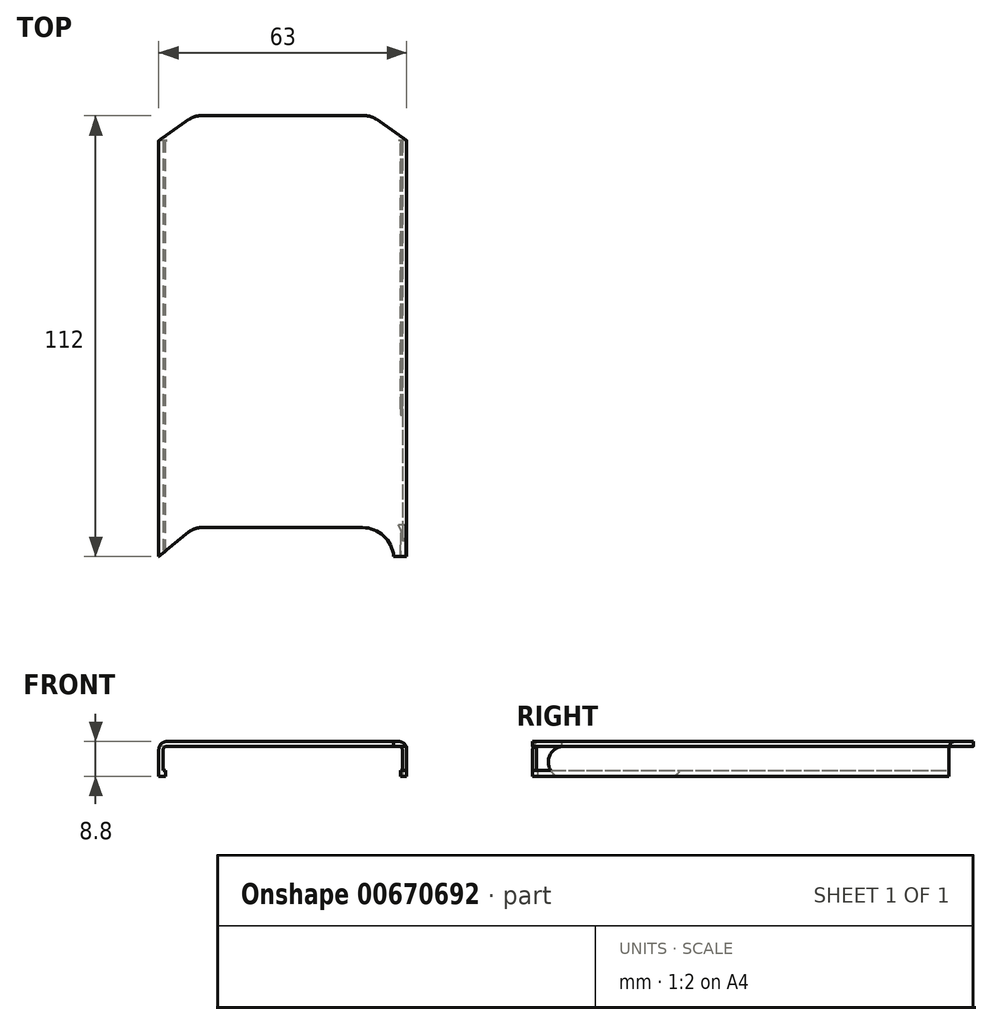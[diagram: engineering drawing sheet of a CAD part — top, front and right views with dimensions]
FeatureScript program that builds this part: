
annotation { "Feature Type Name" : "Feature", "Feature Type Description" : "" }
export const myFeature = defineFeature(function(context is Context, id is Id, definition is map)
    precondition{}
    {
        {
            var Q0;
            Q0=qCreatedBy(makeId("Top.planeOp"),FACE);
            var sketch = newSketch(context, id + "F0", { "sketchPlane" : qUnion([Q0])});
            skLineSegment(sketch, "E0", {"start": v(0, 105.7) * mm, "end": v(7.7, 111.1) * mm});
            skLineSegment(sketch, "E1", {"start": v(10.58, 112) * mm, "end": v(31.5, 112) * mm});
            skLineSegment(sketch, "E2.MirrorCS", {"start": v(52.42, 112) * mm, "end": v(31.5, 112) * mm});
            skLineSegment(sketch, "E3.MirrorCS", {"start": v(63, 105.7) * mm, "end": v(55.3, 111.1) * mm});
            skCircle(sketch, "E4", {"center": v(51.72, -0.65) * mm, "radius": 8 * mm, "construction": true});
            skLineSegment(sketch, "E5", {"start": v(63, 0) * mm, "end": v(59.7, 0) * mm});
            skLineSegment(sketch, "E6", {"start": v(51.72, 7.35) * mm, "end": v(10.78, 7.35) * mm});
            skLineSegment(sketch, "E7", {"start": v(7.62, 6.22) * mm, "end": v(0, 0) * mm});
            skArc(sketch, "E8", {"start": v(59.7, 0) * mm, "mid": v(57.14, 5.23) * mm, "end": v(51.72, 7.35) * mm});
            skPoint(sketch, "E9.visualSharp", {"position": v(9, 7.35) * mm});
            skArc(sketch, "E9.filletArc", {"start": v(10.78, 7.35) * mm, "mid": v(9.1, 7.06) * mm, "end": v(7.62, 6.22) * mm});
            skPoint(sketch, "E10.visualSharp", {"position": v(9, 112) * mm});
            skArc(sketch, "E10.filletArc", {"start": v(10.58, 112) * mm, "mid": v(9.07, 111.77) * mm, "end": v(7.7, 111.1) * mm});
            skPoint(sketch, "E11.visualSharp", {"position": v(54, 112) * mm});
            skArc(sketch, "E11.filletArc", {"start": v(55.3, 111.1) * mm, "mid": v(53.93, 111.77) * mm, "end": v(52.42, 112) * mm});
            skLineSegment(sketch, "E12", {"start": v(0, 0) * mm, "end": v(0, 105.7) * mm});
            skLineSegment(sketch, "E13", {"start": v(63, 105.7) * mm, "end": v(63, 0) * mm});
            skSolve(sketch);
        }
        {
            var Q0;
            Q0 = qSketchRegion(id + "F0", true);
            extrude(context, id + "F1", {"entities" : qUnion([Q0]), "depth" : 1.2 * mm, "offsetDistance" : 25 * mm});
        }
        {
            var Q0;
            Q0=makeQuery(id+"F1.opExtrude","CAP_FACE",FACE,{"disambiguationData":[OSD([sQuery(id+"F0.wireOp",EDGE,"E0"),sQuery(id+"F0.wireOp",EDGE,"E1"),sQuery(id+"F0.wireOp",EDGE,"E2.MirrorCS"),sQuery(id+"F0.wireOp",EDGE,"E3.MirrorCS"),sQuery(id+"F0.wireOp",EDGE,"E5"),sQuery(id+"F0.wireOp",EDGE,"E6"),sQuery(id+"F0.wireOp",EDGE,"E7"),sQuery(id+"F0.wireOp",EDGE,"E8"),sQuery(id+"F0.wireOp",EDGE,"E9.filletArc"),sQuery(id+"F0.wireOp",EDGE,"E10.filletArc"),sQuery(id+"F0.wireOp",EDGE,"E11.filletArc"),sQuery(id+"F0.wireOp",EDGE,"E12"),sQuery(id+"F0.wireOp",EDGE,"E13")])],"isStart":false});
            var sketch = newSketch(context, id + "F2", { "sketchPlane" : qUnion([Q0])});
            skLineSegment(sketch, "E14", {"start": v(1.1, 106.47) * mm, "end": v(1.1, 0.9) * mm});
            skLineSegment(sketch, "E15", {"start": v(61.9, 106.47) * mm, "end": v(61.9, 0) * mm});
            skSolve(sketch);
        }
        {
            var Q0;
            {var subQ0=sQuery(id+"F2.wireOp",EDGE,"E15");Q0=makeQuery(id+"F2.imprint","IMPRINT",FACE,{"disambiguationData":[TD([[makeQuery(id+"F2.imprint","IMPRINT",EDGE,{"derivedFrom":subQ0}),1.0]])]});}
            var Q1;
            {var subQ0=sQuery(id+"F2.wireOp",EDGE,"E14");Q1=makeQuery(id+"F2.imprint","IMPRINT",FACE,{"disambiguationData":[TD([[makeQuery(id+"F2.imprint","IMPRINT",EDGE,{"derivedFrom":subQ0}),-1.0]])]});}
            extrude(context, id + "F3", {"entities" : qUnion([Q0, Q1]), "operationType" : NewBodyOperationType.ADD, "oppositeDirection" : true, "depth" : 8.8 * mm, "offsetDistance" : 25 * mm});
        }
        {
            var Q0;
            {var subQ0=sQuery(id+"F0.wireOp",EDGE,"E12");Q0=makeQuery(id+"F3.boolean.opBoolean","MERGE",FACE,{"derivedFrom":[makeQuery(id+"F1.opExtrude","SWEPT_FACE",FACE,{"disambiguationData":[OSD([subQ0])]}),makeQuery(id+"F3.opExtrude","SWEPT_FACE",FACE,{"disambiguationData":[OSD([subQ0])]})]});}
            var sketch = newSketch(context, id + "F4", { "sketchPlane" : qUnion([Q0])});
            skLineSegment(sketch, "E16", {"start": v(0, 0) * mm, "end": v(0, -7.6) * mm});
            skLineSegment(sketch, "E17", {"start": v(0, -7.6) * mm, "end": v(-105.7, -7.6) * mm});
            skLineSegment(sketch, "E18", {"start": v(0, -6.1) * mm, "end": v(-105.7, -6.1) * mm});
            skSolve(sketch);
        }
        {
            var Q0;
            {var subQ0=sQuery(id+"F4.wireOp",EDGE,"E17");Q0=makeQuery(id+"F4.imprint","IMPRINT",FACE,{"disambiguationData":[TD([[makeQuery(id+"F4.imprint","IMPRINT",EDGE,{"derivedFrom":subQ0}),-1.0]])]});}
            extrude(context, id + "F5", {"entities" : qUnion([Q0]), "operationType" : NewBodyOperationType.ADD, "oppositeDirection" : true, "depth" : 1.7 * mm, "offsetDistance" : 25 * mm});
        }
        {
            var Q0;
            Q0=makeQuery(id+"F5.opExtrude","SWEPT_FACE",FACE,{"disambiguationData":[OSD([sQuery(id+"F4.wireOp",EDGE,"E18")])]});
            var sketch = newSketch(context, id + "F6", { "sketchPlane" : qUnion([Q0])});
            skLineSegment(sketch, "E19", {"start": v(1.1, 0.9) * mm, "end": v(1.7, 1.39) * mm});
            skSolve(sketch);
        }
        {
            var Q0;
            {var subQ0=sQuery(id+"F6.wireOp",EDGE,"E19");Q0=makeQuery(id+"F6.imprint","IMPRINT",FACE,{"disambiguationData":[TD([[makeQuery(id+"F6.imprint","IMPRINT",EDGE,{"derivedFrom":subQ0}),-1.0]])]});}
            extrude(context, id + "F7", {"entities" : qUnion([Q0]), "operationType" : NewBodyOperationType.REMOVE, "oppositeDirection" : true, "depth" : 25 * mm, "offsetDistance" : 25 * mm});
        }
        {
            var Q0;
            Q0=makeQuery(id+"F5.boolean.opBoolean","MERGE",FACE,{"derivedFrom":[makeQuery(id+"F3.opExtrude","CAP_FACE",FACE,{"disambiguationData":[OSD([sQuery(id+"F0.wireOp",EDGE,"E0"),sQuery(id+"F0.wireOp",EDGE,"E7"),sQuery(id+"F0.wireOp",EDGE,"E12"),sQuery(id+"F2.wireOp",EDGE,"E14")])],"isStart":false}),makeQuery(id+"F5.opExtrude","SWEPT_FACE",FACE,{"disambiguationData":[OSD([sQuery(id+"F4.wireOp",EDGE,"E17")])]})]});
            var sketch = newSketch(context, id + "F8", { "sketchPlane" : qUnion([Q0])});
            skLineSegment(sketch, "E20", {"start": v(1.1, -105.7) * mm, "end": v(0, -105.7) * mm});
            skSolve(sketch);
        }
        {
            var Q0;
            Q0=makeQuery(id+"F8.imprint","IMPRINT",FACE,{"disambiguationData":[TD([[makeQuery(id+"F8.imprint","IMPRINT",EDGE,{"derivedFrom":sQuery(id+"F8.wireOp",EDGE,"E20")}),1.0]])]});
            extrude(context, id + "F9", {"entities" : qUnion([Q0]), "operationType" : NewBodyOperationType.REMOVE, "oppositeDirection" : true, "depth" : 7.6 * mm, "offsetDistance" : 25 * mm});
        }
        {
            var Q0;
            Q0=makeQuery(id+"F3.opExtrude","CAP_FACE",FACE,{"disambiguationData":[OSD([sQuery(id+"F0.wireOp",EDGE,"E3.MirrorCS"),sQuery(id+"F0.wireOp",EDGE,"E5"),sQuery(id+"F0.wireOp",EDGE,"E13"),sQuery(id+"F2.wireOp",EDGE,"E15")])],"isStart":false});
            var sketch = newSketch(context, id + "F10", { "sketchPlane" : qUnion([Q0])});
            skLineSegment(sketch, "E21", {"start": v(63, -105.7) * mm, "end": v(61.9, -105.7) * mm});
            skSolve(sketch);
        }
        {
            var Q0;
            {var subQ0=sQuery(id+"F10.wireOp",EDGE,"E21");Q0=makeQuery(id+"F10.imprint","IMPRINT",FACE,{"disambiguationData":[TD([[makeQuery(id+"F10.imprint","IMPRINT",EDGE,{"derivedFrom":subQ0}),1.0]])]});}
            extrude(context, id + "F11", {"entities" : qUnion([Q0]), "operationType" : NewBodyOperationType.REMOVE, "oppositeDirection" : true, "depth" : 7.6 * mm, "offsetDistance" : 25 * mm});
        }
        {
            var Q0;
            Q0=makeQuery(id+"F3.opExtrude","SWEPT_FACE",FACE,{"disambiguationData":[OSD([sQuery(id+"F2.wireOp",EDGE,"E15")])]});
            var sketch = newSketch(context, id + "F12", { "sketchPlane" : qUnion([Q0])});
            skLineSegment(sketch, "E22", {"start": v(0, -7.6) * mm, "end": v(-105.7, -7.6) * mm, "construction": true});
            skLineSegment(sketch, "E23", {"start": v(-105.7, -7.6) * mm, "end": v(-105.7, 0) * mm});
            skLineSegment(sketch, "E24", {"start": v(0, -6.1) * mm, "end": v(-4.5, -6.1) * mm});
            skLineSegment(sketch, "E25", {"start": v(-4, -7.6) * mm, "end": v(0, -7.6) * mm});
            skArc(sketch, "E26", {"start": v(-8, 0) * mm, "mid": v(-4.08, -3.04) * mm, "end": v(-6.05, -7.6) * mm});
            skLineSegment(sketch, "E27", {"start": v(0, -7.6) * mm, "end": v(-6.05, -7.6) * mm});
            skArc(sketch, "E28", {"start": v(-34, 0) * mm, "mid": v(-37.92, -3.04) * mm, "end": v(-35.95, -7.6) * mm});
            skLineSegment(sketch, "E29", {"start": v(-37.5, -6.1) * mm, "end": v(-105.7, -6.1) * mm});
            skLineSegment(sketch, "E30", {"start": v(-105.7, -7.6) * mm, "end": v(-35.95, -7.6) * mm});
            skSolve(sketch);
        }
        {
            var Q0;
            {var subQ7=sQuery(id+"F12.wireOp",EDGE,"E26");var subQ8=makeQuery(id+"F12.imprint","INTERSECT",VERTEX,{"derivedFrom":[sQuery(id+"F12.wireOp",EDGE,"E24"),subQ7]});Q0=makeQuery(id+"F12.imprint","IMPRINT",FACE,{"disambiguationData":[TD([[makeQuery(id+"F12.imprint","IMPRINT",EDGE,{"disambiguationData":[TD([[subQ8,-1.0]])],"derivedFrom":subQ7}),-1.0]])]});}
            extrude(context, id + "F13", {"entities" : qUnion([Q0]), "operationType" : NewBodyOperationType.REMOVE, "oppositeDirection" : true, "depth" : 25 * mm, "offsetDistance" : 25 * mm});
        }
        {
            var Q0;
            {var subQ2=sQuery(id+"F12.wireOp",EDGE,"E29");Q0=makeQuery(id+"F12.imprint","IMPRINT",FACE,{"disambiguationData":[TD([[makeQuery(id+"F12.imprint","IMPRINT",EDGE,{"derivedFrom":subQ2}),1.0]])]});}
            var Q1;
            {var subQ0=sQuery(id+"F12.wireOp",EDGE,"E24");Q1=makeQuery(id+"F12.imprint","IMPRINT",FACE,{"disambiguationData":[TD([[makeQuery(id+"F12.imprint","IMPRINT",EDGE,{"derivedFrom":subQ0}),1.0]])]});}
            extrude(context, id + "F14", {"entities" : qUnion([Q0, Q1]), "operationType" : NewBodyOperationType.ADD, "depth" : .5 * mm, "offsetDistance" : 25 * mm});
        }
        {
            var Q0;
            Q0=makeQuery(id+"F3.boolean.opBoolean","INTERSECT",EDGE,{"derivedFrom":[makeQuery(id+"F1.opExtrude","CAP_FACE",FACE,{"disambiguationData":[OSD([sQuery(id+"F0.wireOp",EDGE,"E0"),sQuery(id+"F0.wireOp",EDGE,"E1"),sQuery(id+"F0.wireOp",EDGE,"E2.MirrorCS"),sQuery(id+"F0.wireOp",EDGE,"E3.MirrorCS"),sQuery(id+"F0.wireOp",EDGE,"E5"),sQuery(id+"F0.wireOp",EDGE,"E6"),sQuery(id+"F0.wireOp",EDGE,"E7"),sQuery(id+"F0.wireOp",EDGE,"E8"),sQuery(id+"F0.wireOp",EDGE,"E9.filletArc"),sQuery(id+"F0.wireOp",EDGE,"E10.filletArc"),sQuery(id+"F0.wireOp",EDGE,"E11.filletArc"),sQuery(id+"F0.wireOp",EDGE,"E12"),sQuery(id+"F0.wireOp",EDGE,"E13")])],"isStart":true}),makeQuery(id+"F3.opExtrude","SWEPT_FACE",FACE,{"disambiguationData":[OSD([sQuery(id+"F2.wireOp",EDGE,"E14")])]})]});
            var Q1;
            {var subQ0=sQuery(id+"F0.wireOp",EDGE,"E5");var subQ1=sQuery(id+"F2.wireOp",EDGE,"E15");var subQ2=makeQuery(id+"F3.opExtrude","SWEPT_FACE",FACE,{"disambiguationData":[OSD([subQ1])]});var subQ3=sQuery(id+"F0.wireOp",EDGE,"E13");var subQ4=sQuery(id+"F0.wireOp",EDGE,"E12");var subQ5=sQuery(id+"F0.wireOp",EDGE,"E11.filletArc");var subQ6=sQuery(id+"F0.wireOp",EDGE,"E10.filletArc");var subQ7=sQuery(id+"F0.wireOp",EDGE,"E9.filletArc");var subQ8=sQuery(id+"F0.wireOp",EDGE,"E8");var subQ9=sQuery(id+"F0.wireOp",EDGE,"E7");var subQ10=sQuery(id+"F0.wireOp",EDGE,"E6");var subQ11=sQuery(id+"F0.wireOp",EDGE,"E3.MirrorCS");var subQ12=sQuery(id+"F0.wireOp",EDGE,"E2.MirrorCS");var subQ13=sQuery(id+"F0.wireOp",EDGE,"E1");var subQ14=sQuery(id+"F0.wireOp",EDGE,"E0");var subQ15=makeQuery(id+"F1.opExtrude","CAP_FACE",FACE,{"disambiguationData":[OSD([subQ14,subQ13,subQ12,subQ11,subQ0,subQ10,subQ9,subQ8,subQ7,subQ6,subQ5,subQ4,subQ3])],"isStart":true});Q1=makeQuery(id+"F13.boolean.opBoolean","SPLIT",EDGE,{"disambiguationData":[TD([makeQuery(id+"F1.opExtrude","SWEPT_FACE",FACE,{"disambiguationData":[OSD([subQ0])]})])],"derivedFrom":makeQuery(id+"F3.boolean.opBoolean","INTERSECT",EDGE,{"derivedFrom":[subQ15,subQ2]})});}
            var Q2;
            {var subQ0=sQuery(id+"F2.wireOp",EDGE,"E15");var subQ1=makeQuery(id+"F3.opExtrude","SWEPT_FACE",FACE,{"disambiguationData":[OSD([subQ0])]});var subQ2=sQuery(id+"F0.wireOp",EDGE,"E13");var subQ3=sQuery(id+"F0.wireOp",EDGE,"E12");var subQ4=sQuery(id+"F0.wireOp",EDGE,"E11.filletArc");var subQ5=sQuery(id+"F0.wireOp",EDGE,"E10.filletArc");var subQ6=sQuery(id+"F0.wireOp",EDGE,"E9.filletArc");var subQ7=sQuery(id+"F0.wireOp",EDGE,"E8");var subQ8=sQuery(id+"F0.wireOp",EDGE,"E7");var subQ9=sQuery(id+"F0.wireOp",EDGE,"E6");var subQ10=sQuery(id+"F0.wireOp",EDGE,"E5");var subQ11=sQuery(id+"F0.wireOp",EDGE,"E3.MirrorCS");var subQ12=sQuery(id+"F0.wireOp",EDGE,"E2.MirrorCS");var subQ13=sQuery(id+"F0.wireOp",EDGE,"E1");var subQ14=sQuery(id+"F0.wireOp",EDGE,"E0");var subQ15=makeQuery(id+"F1.opExtrude","CAP_FACE",FACE,{"disambiguationData":[OSD([subQ14,subQ13,subQ12,subQ11,subQ10,subQ9,subQ8,subQ7,subQ6,subQ5,subQ4,subQ3,subQ2])],"isStart":true});Q2=makeQuery(id+"F13.boolean.opBoolean","SPLIT",EDGE,{"disambiguationData":[TD([makeQuery(id+"F11.boolean.opBoolean","COPY",FACE,{"derivedFrom":makeQuery(id+"F11.opExtrude","SWEPT_FACE",FACE,{"disambiguationData":[OSD([sQuery(id+"F10.wireOp",EDGE,"E21")])]})})])],"derivedFrom":makeQuery(id+"F3.boolean.opBoolean","INTERSECT",EDGE,{"derivedFrom":[subQ15,subQ1]})});}
            fillet(context, id + "F15", {"entities" : qUnion([Q0, Q1, Q2]), "radius" : 1 * mm, "tangentPropagation" : true, "allowEdgeOverflow" : false});
        }
        {
            var Q0;
            Q0=makeQuery(id+"F1.opExtrude","CAP_EDGE",EDGE,{"disambiguationData":[OSD([sQuery(id+"F0.wireOp",EDGE,"E13")])],"isStart":false});
            var Q1;
            Q1=makeQuery(id+"F1.opExtrude","CAP_EDGE",EDGE,{"disambiguationData":[OSD([sQuery(id+"F0.wireOp",EDGE,"E12")])],"isStart":false});
            fillet(context, id + "F16", {"entities" : qUnion([Q0, Q1]), "radius" : 2 * mm, "tangentPropagation" : true, "allowEdgeOverflow" : false});
        }
    });
